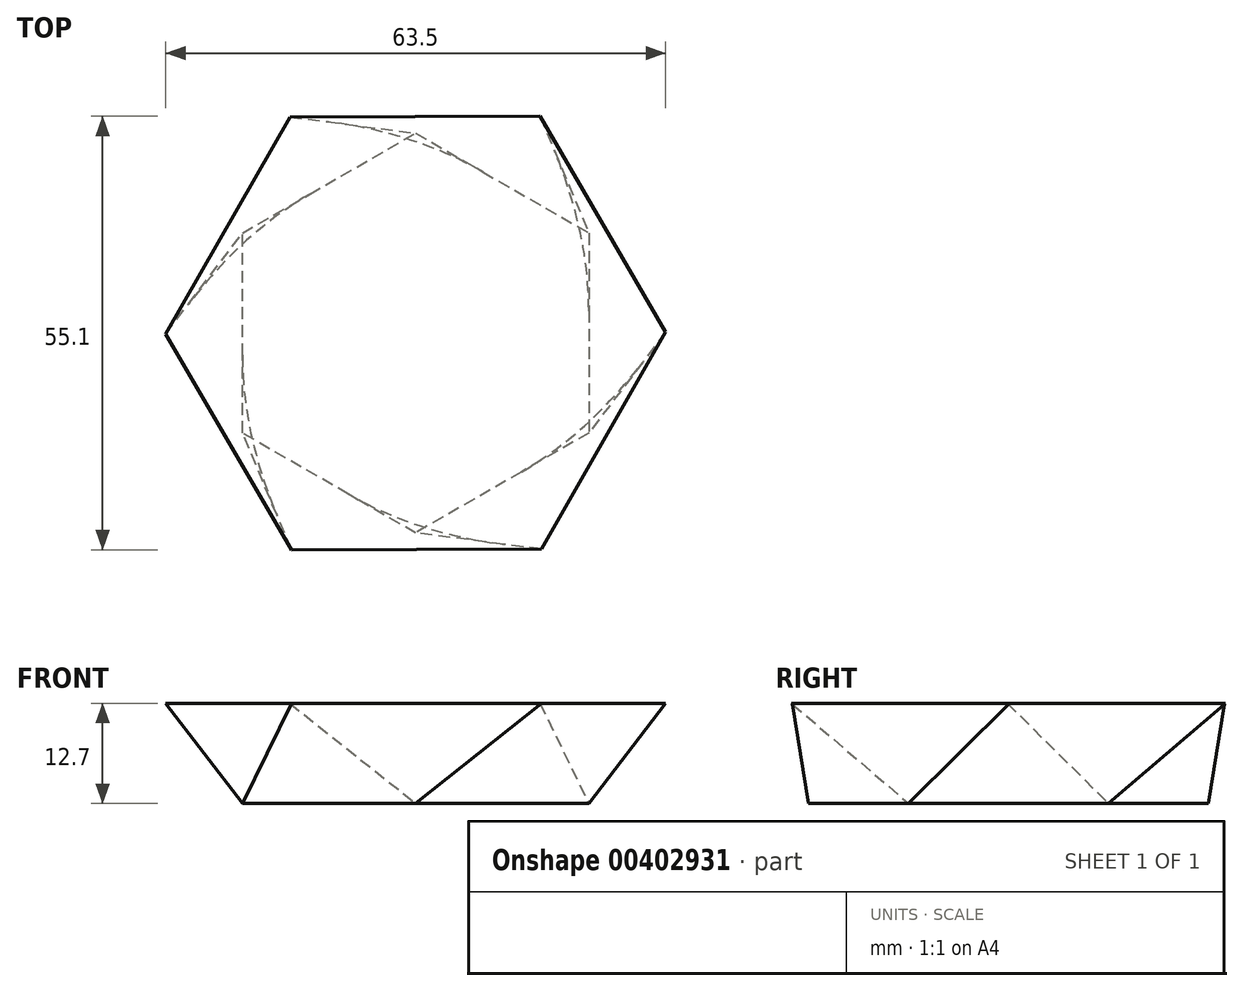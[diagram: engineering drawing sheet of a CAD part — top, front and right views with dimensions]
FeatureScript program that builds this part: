
annotation { "Feature Type Name" : "Feature", "Feature Type Description" : "" }
export const myFeature = defineFeature(function(context is Context, id is Id, definition is map)
    precondition{}
    {
        {
            var Q0;
            Q0=qCreatedBy(makeId("Top.planeOp"),FACE);
            var sketch = newSketch(context, id + "F0", { "sketchPlane" : qUnion([Q0])});
            skCircle(sketch, "E0.cCircle", {"center": v(0, 0) * mm, "radius": 22 * mm, "construction": true});
            skLineSegment(sketch, "E0.0", {"start": v(22, 12.7) * mm, "end": v(22, -12.7) * mm});
            skLineSegment(sketch, "E0.1", {"start": v(22, -12.7) * mm, "end": v(0, -25.4) * mm});
            skLineSegment(sketch, "E0.2", {"start": v(0, -25.4) * mm, "end": v(-22, -12.7) * mm});
            skLineSegment(sketch, "E0.3", {"start": v(-22, -12.7) * mm, "end": v(-22, 12.7) * mm});
            skLineSegment(sketch, "E0.4", {"start": v(-22, 12.7) * mm, "end": v(0, 25.4) * mm});
            skLineSegment(sketch, "E0.5", {"start": v(0, 25.4) * mm, "end": v(22, 12.7) * mm});
            skPoint(sketch, "E0.0.midPoint", {"position": v(22, 0) * mm});
            skSolve(sketch);
        }
        {
            var Q0;
            Q0=qCreatedBy(makeId("Top.planeOp"),FACE);
            cPlane(context, id + "F1", {"entities" : qUnion([Q0]), "cplaneType" : CPlaneType.OFFSET, "offset" : 12.7 * mm, "width" : 152.4 * mm, "height" : 152.4 * mm});
        }
        {
            var Q0;
            Q0=qCreatedBy(id+"F1.planeOp",FACE);
            var sketch = newSketch(context, id + "F2", { "sketchPlane" : qUnion([Q0])});
            skCircle(sketch, "E1.cCircle", {"center": v(0, 0) * mm, "radius": 27.5 * mm, "construction": true});
            skLineSegment(sketch, "E1.0", {"start": v(15.78, 27.55) * mm, "end": v(31.75, 0.1) * mm});
            skLineSegment(sketch, "E1.1", {"start": v(31.75, 0.1) * mm, "end": v(15.97, -27.44) * mm});
            skLineSegment(sketch, "E1.2", {"start": v(15.97, -27.44) * mm, "end": v(-15.78, -27.55) * mm});
            skLineSegment(sketch, "E1.3", {"start": v(-15.78, -27.55) * mm, "end": v(-31.75, -0.1) * mm});
            skLineSegment(sketch, "E1.4", {"start": v(-31.75, -0.1) * mm, "end": v(-15.97, 27.44) * mm});
            skLineSegment(sketch, "E1.5", {"start": v(-15.97, 27.44) * mm, "end": v(15.78, 27.55) * mm});
            skPoint(sketch, "E1.0.midPoint", {"position": v(23.77, 13.83) * mm});
            skSolve(sketch);
        }
        {
            var Q0;
            Q0=makeQuery(id+"F2.imprint","IMPRINT",FACE,{"disambiguationData":[TD([[makeQuery(id+"F2.imprint","IMPRINT",EDGE,{"derivedFrom":sQuery(id+"F2.wireOp",EDGE,"E1.0")}),-1.0]])]});
            var Q1;
            Q1=makeQuery(id+"F0.imprint","IMPRINT",FACE,{"disambiguationData":[TD([[makeQuery(id+"F0.imprint","IMPRINT",EDGE,{"derivedFrom":sQuery(id+"F0.wireOp",EDGE,"E0.0")}),-1.0]])]});
            var Q2;
            Q2=sQuery(id+"F2.wireOp",VERTEX,"E1.1.start");
            var Q3;
            Q3=sQuery(id+"F0.wireOp",VERTEX,"E0.1.start");
            loft(context, id + "F3", {"sheetProfilesArray" : [{ "sheetProfileEntities" : qUnion([Q0]) }, { "sheetProfileEntities" : qUnion([Q1]) }], "matchConnections" : true, "connections" : [{ "connectionEntities" : qUnion([Q2, Q3]), "connectionEdgeQueries" : qUnion([]), "connectionEdgeParameters" : [] }]});
        }
    });
